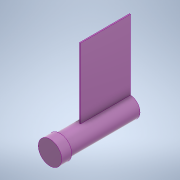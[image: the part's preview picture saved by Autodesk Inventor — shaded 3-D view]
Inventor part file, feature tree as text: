
AUTODESK INVENTOR PART (.ipt)
format: ipt  version: 2021.2 (Build 252289000, 289)  size: 118,272 bytes
history: native  units: in
note: dims shown in document units (in); Inventor stores cm internally (conversion verified against a paired STEP export)
features: extrude x3, sketch x3
ambient origin geometry x8: Origin, YZ Plane, XZ Plane, XY Plane, X Axis, Y Axis, Z Axis, Center Point
bodies: Solid1 (feature_tree)
feature tree (6):
  extrude  "Extrusion1"  Depth=2.0in TaperAngle=0.0deg
  extrude  "Extrusion3"  Depth=0.25in TaperAngle=0.0deg
  extrude  "Extrusion4"  Depth=2.0in
  sketch  "Sketch1"  dims[d0=0.5in d1=2.0in d2=0.0in]
  sketch  "Sketch2"  dims[d3=0.585in d6=0.25in d7=0.0in]
  sketch  "Sketch3"  dims[d8=0.75in d9=2.0in d10=0.025in d11=0.0in]
